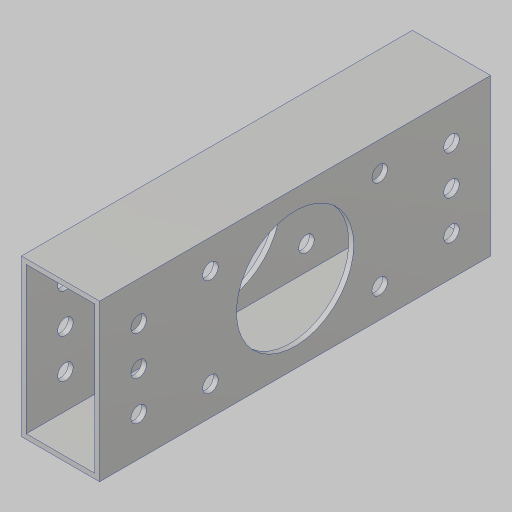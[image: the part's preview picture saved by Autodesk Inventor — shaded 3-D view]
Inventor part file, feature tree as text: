
AUTODESK INVENTOR PART (.ipt)
format: ipt  version: 2023.5 (Build 275446000, 446)  size: 166,400 bytes
history: native  units: in
note: dims shown in document units (in); Inventor stores cm internally (conversion verified against a paired STEP export)
features: extrude x2, sketch x2, hole x1
ambient origin geometry x8: Origin, YZ Plane, XZ Plane, XY Plane, X Axis, Y Axis, Z Axis, Center Point
bodies: Solid1 (feature_tree)
feature tree (5):
  extrude  "Extrusion1"  Depth=2.5in
  hole  "Hole1"  [1 undecoded]
  extrude  "Extrusion2"  Depth=0.5in
  sketch  "Sketch2"  dims[d4=0.0in d5=2.5in]
  sketch  "Sketch3"  dims[d6=2.3622in d8=360.0deg d10=0.201in d11=0.75in d12=0.385in d13=0.25in d14=0.5635in d15=1.0in d16=0.8108in d17=0.5in d18=0.5in d19=0.5in d20=1.5in d21=1.0in d22=0.0in]
note: 1 required parameter value undecoded (feature->parameter linkage not recoverable at this tier; creation-order binding heuristic only, values carry confidence <= 0.55)
